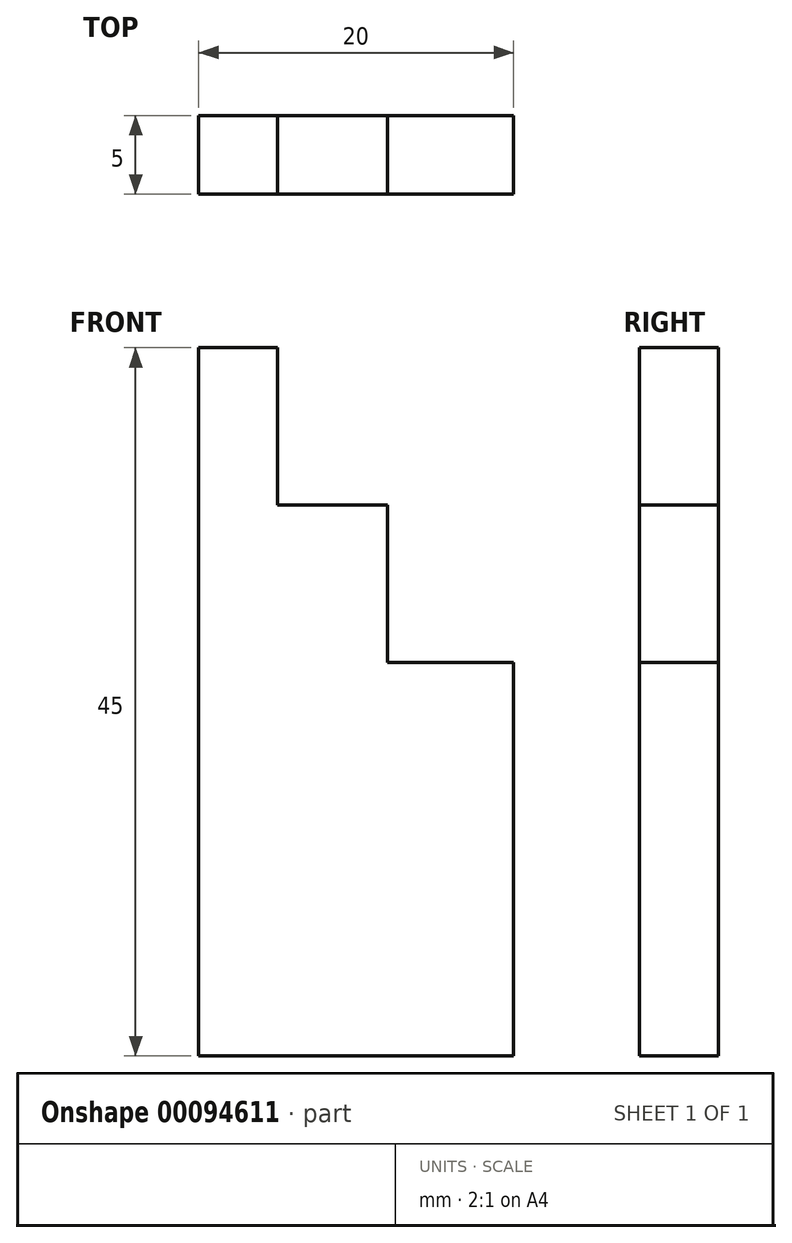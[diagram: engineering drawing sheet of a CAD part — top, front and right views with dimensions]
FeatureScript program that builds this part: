
annotation { "Feature Type Name" : "Feature", "Feature Type Description" : "" }
export const myFeature = defineFeature(function(context is Context, id is Id, definition is map)
    precondition{}
    {
        {
            var Q0;
            Q0=qCreatedBy(makeId("Front.planeOp"),FACE);
            var sketch = newSketch(context, id + "F0", { "sketchPlane" : qUnion([Q0])});
            skLineSegment(sketch, "E0", {"start": v(0, 0) * mm, "end": v(20, 0) * mm});
            skLineSegment(sketch, "E1", {"start": v(20, 0) * mm, "end": v(20, 25) * mm});
            skLineSegment(sketch, "E2", {"start": v(20, 25) * mm, "end": v(12, 25) * mm});
            skLineSegment(sketch, "E3", {"start": v(12, 25) * mm, "end": v(12, 35) * mm});
            skLineSegment(sketch, "E4", {"start": v(12, 35) * mm, "end": v(5, 35) * mm});
            skLineSegment(sketch, "E5", {"start": v(5, 35) * mm, "end": v(5, 45) * mm});
            skLineSegment(sketch, "E6", {"start": v(5, 45) * mm, "end": v(0, 45) * mm});
            skLineSegment(sketch, "E7", {"start": v(0, 45) * mm, "end": v(0, 0) * mm});
            skSolve(sketch);
        }
        {
            var Q0;
            Q0=makeQuery(id+"F0.imprint","IMPRINT",FACE,{"disambiguationData":[TD([[makeQuery(id+"F0.imprint","IMPRINT",EDGE,{"derivedFrom":sQuery(id+"F0.wireOp",EDGE,"E0")}),1.0]])]});
            extrude(context, id + "F1", {"entities" : qUnion([Q0]), "depth" : 5 * mm});
        }
    });
